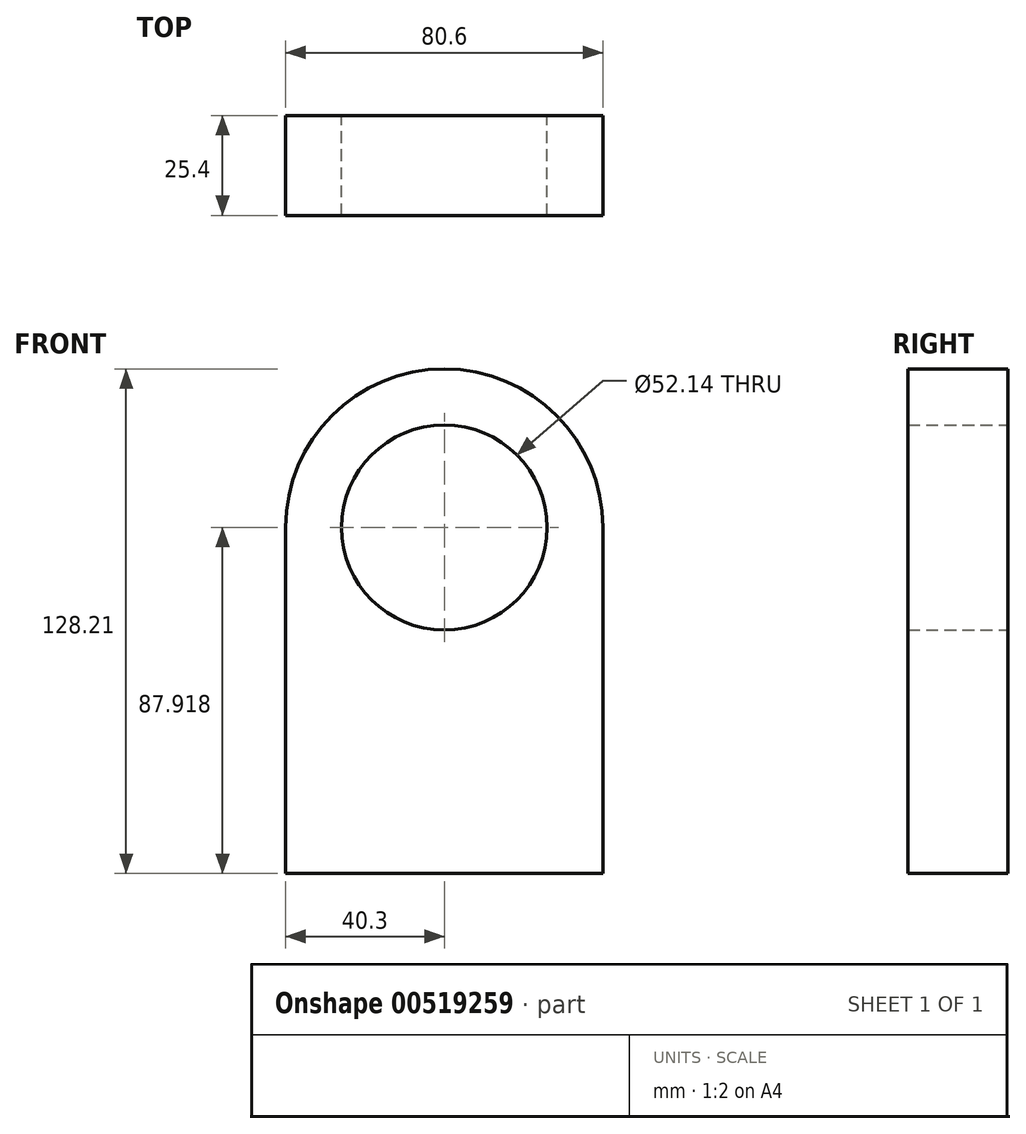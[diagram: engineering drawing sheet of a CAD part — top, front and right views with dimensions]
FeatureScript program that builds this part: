
annotation { "Feature Type Name" : "Feature", "Feature Type Description" : "" }
export const myFeature = defineFeature(function(context is Context, id is Id, definition is map)
    precondition{}
    {
        {
            var Q0;
            Q0=qCreatedBy(makeId("Front.planeOp"),FACE);
            var sketch = newSketch(context, id + "F0", { "sketchPlane" : qUnion([Q0])});
            skLineSegment(sketch, "E0.top", {"start": v(-40.3, -43.96) * mm, "end": v(40.3, -43.96) * mm});
            skLineSegment(sketch, "E0.left", {"start": v(-40.3, 43.96) * mm, "end": v(-40.3, -43.96) * mm});
            skLineSegment(sketch, "E0.right", {"start": v(40.3, 43.96) * mm, "end": v(40.3, -43.96) * mm});
            skPoint(sketch, "E0.middle", {"position": v(0, 0) * mm});
            skCircle(sketch, "E1", {"center": v(0, 43.96) * mm, "radius": 40.3 * mm});
            skCircle(sketch, "E2.0", {"center": v(0, 43.96) * mm, "radius": 26.07 * mm});
            skSolve(sketch);
        }
        {
            var Q0;
            Q0=makeQuery(id+"F0.imprint","IMPRINT",FACE,{"disambiguationData":[TD([[makeQuery(id+"F0.imprint","IMPRINT",EDGE,{"derivedFrom":sQuery(id+"F0.wireOp",EDGE,"E0.top")}),1.0]])]});
            var Q1;
            Q1=makeQuery(id+"F0.imprint","IMPRINT",FACE,{"disambiguationData":[TD([[makeQuery(id+"F0.imprint","IMPRINT",EDGE,{"derivedFrom":sQuery(id+"F0.wireOp",EDGE,"E2.0")}),-1.0]])]});
            extrude(context, id + "F1", {"entities" : qUnion([Q0, Q1]), "depth" : 25.4 * mm, "offsetDistance" : 25.4 * mm});
        }
    });
